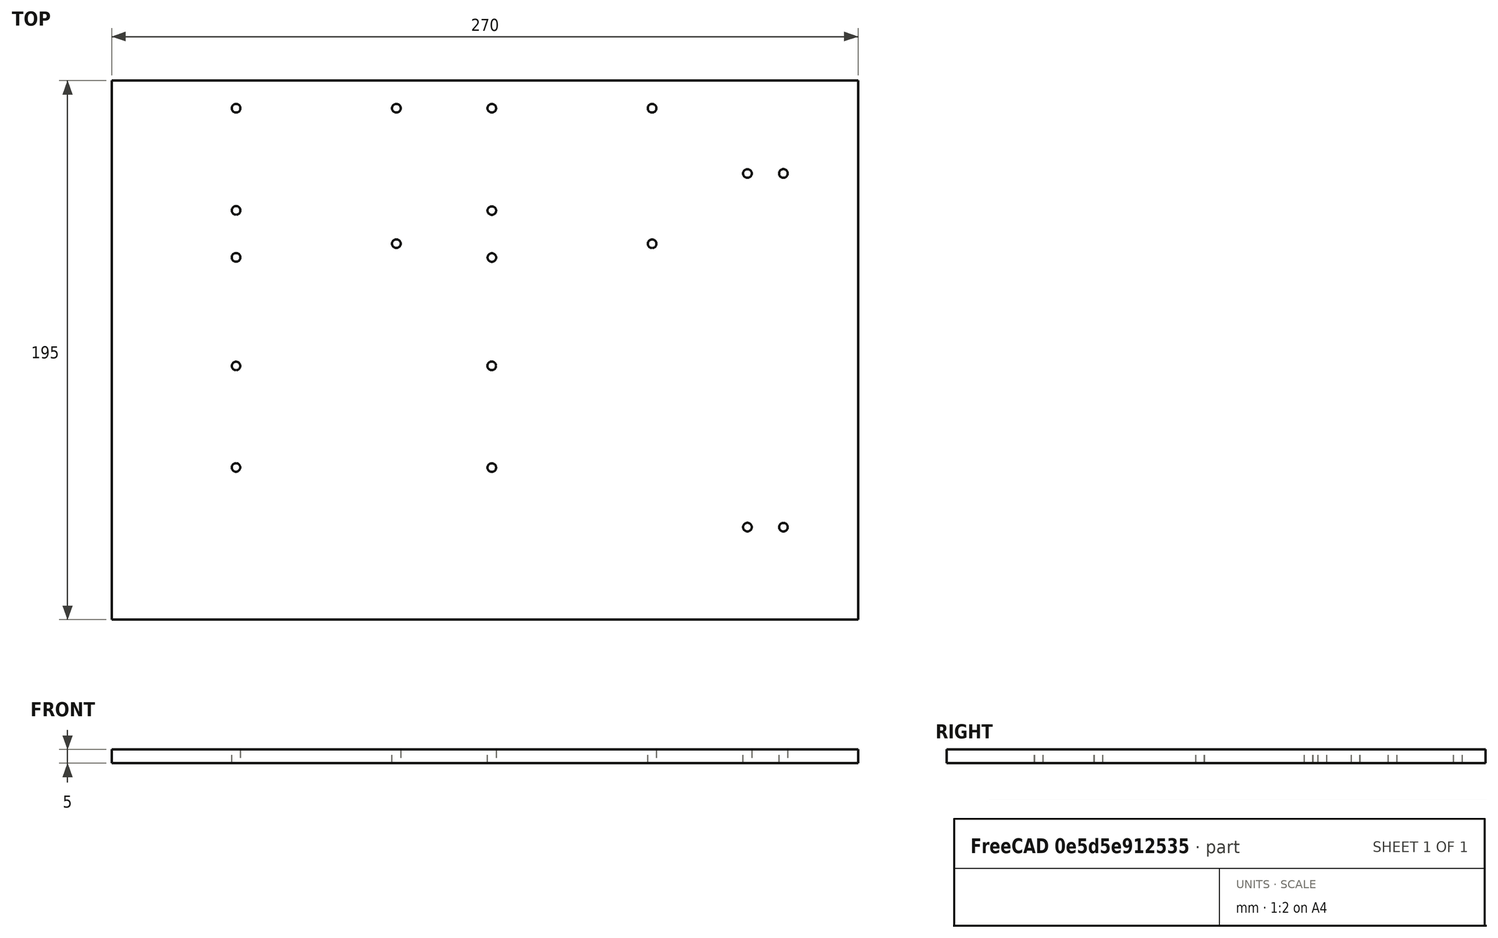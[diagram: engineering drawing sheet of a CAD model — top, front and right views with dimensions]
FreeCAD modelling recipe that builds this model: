
FCSTD DOCUMENT  (FreeCAD 0.16R6710 (Git))
Label: glassDesignQuarter
License: All rights reserved
LicenseURL: http://en.wikipedia.org/wiki/All_rights_reserved
objects: Drawing::FeatureViewPython×34, App::DocumentObjectGroup×5, Drawing::FeatureViewPart×2, Part::Box×1, Sketcher::SketchObject×1, PartDesign::Pocket×1, Drawing::FeaturePage×1
note: 4 computed .brp shape members not serialized (recipe doc carries the construction recipe); baked Part::Feature solids carry a one-line shape summary decoded from their .brp

FEATURE [Part::Box] Box002  label="1/4"
  Height = 5
  Length = 270
  Width = 195
FEATURE [Sketcher::SketchObject] Sketch032
  Placement = pos=(0,0,5) rot=(0,0,1;0rad)
  Support = -> Box002 [Face6]
  sketch-geometry (18):
    g0: Circle CenterX=45.0007 CenterY=185.02 CenterZ=0 NormalX=0 NormalY=0 NormalZ=1 Radius=1.5637
    g1: Circle CenterX=45.0164 CenterY=148.036 CenterZ=0 NormalX=0 NormalY=0 NormalZ=1 Radius=1.56346
    g2: Circle CenterX=44.9788 CenterY=131.047 CenterZ=0 NormalX=0 NormalY=0 NormalZ=1 Radius=1.57064
    g3: Circle CenterX=102.99 CenterY=185.022 CenterZ=0 NormalX=0 NormalY=0 NormalZ=1 Radius=1.5747
    g4: Circle CenterX=137.501 CenterY=185.021 CenterZ=0 NormalX=0 NormalY=0 NormalZ=1 Radius=1.55657
    g5: Circle CenterX=102.965 CenterY=136.023 CenterZ=0 NormalX=0 NormalY=0 NormalZ=1 Radius=1.56664
    g6: Circle CenterX=195.466 CenterY=185.025 CenterZ=0 NormalX=0 NormalY=0 NormalZ=1 Radius=1.56353
    g7: Circle CenterX=137.498 CenterY=147.976 CenterZ=0 NormalX=0 NormalY=0 NormalZ=1 Radius=1.55376
    g8: Circle CenterX=137.521 CenterY=130.994 CenterZ=0 NormalX=0 NormalY=0 NormalZ=1 Radius=1.55586
    g9: Circle CenterX=44.9819 CenterY=91.7501 CenterZ=0 NormalX=0 NormalY=0 NormalZ=1 Radius=1.53762
    g10: Circle CenterX=137.481 CenterY=91.7836 CenterZ=0 NormalX=0 NormalY=0 NormalZ=1 Radius=1.5579
    g11: Circle CenterX=44.9591 CenterY=55.0195 CenterZ=0 NormalX=0 NormalY=0 NormalZ=1 Radius=1.55028
    g12: Circle CenterX=137.5 CenterY=54.971 CenterZ=0 NormalX=0 NormalY=0 NormalZ=1 Radius=1.5621
    g13: Circle CenterX=195.5 CenterY=135.972 CenterZ=0 NormalX=0 NormalY=0 NormalZ=1 Radius=1.5583
    g14: Circle CenterX=229.972 CenterY=161.408 CenterZ=0 NormalX=0 NormalY=0 NormalZ=1 Radius=1.56999
    g15: Circle CenterX=242.978 CenterY=161.431 CenterZ=0 NormalX=0 NormalY=0 NormalZ=1 Radius=1.57387
    g16: Circle CenterX=229.973 CenterY=33.4261 CenterZ=0 NormalX=0 NormalY=0 NormalZ=1 Radius=1.57027
    g17: Circle CenterX=242.986 CenterY=33.4186 CenterZ=0 NormalX=0 NormalY=0 NormalZ=1 Radius=1.55472
FEATURE [PartDesign::Pocket] Pocket002
  Length = 5
  Sketch = -> Sketch032
  Type = 0
FEATURE [App::DocumentObjectGroup] Group  label="1/4U"
  Group = -> [Box002,Pocket002]
FEATURE [Drawing::FeatureViewPart] Ortho  label="Ortho_0_0"
  Direction = (0,0,1)
  HiddenWidth = 0.15
  LineWidth = 0.35
  Rotation = 0
  ShowHiddenLines = false
  ShowSmoothLines = false
  Source = -> Pocket002
  Tolerance = 0.05
  ViewResult = <g id="Ortho_0_0"\n   transform="rotate(0,120,297.67) translate(120,297.67) scale(1,1)"\n  >\n<g   stroke="rgb(0, 0, 0)"\n   stroke-width="0.35"\n   stroke-linecap="butt"\n   stroke-linejoin="miter"\n   fill="none"\n   transform="scale(1,-1)"\n  >\n<path id= "1" d=" M 0 0 L 0 195 " />\n<path id= "2" d=" M 0 0 L 270 0 " />\n<path id= "3" d=" M 0 195 L 270 195 " />\n<path id= "4" d=" M 270 0 L 270 195 " />\n<circle cx ="45.0164" cy ="148.036" r ="1.56346" /><circle cx ="44.9788" cy ="131.047" r ="1.57064" /><circle cx ="137.498" cy ="147.976" r ="1.55376" /><circle cx ="137.521" cy ="130.994" r ="1.55586" /><circle cx ="102.965" cy ="136.023" r ="1.56664" /><circle cx ="137.5" cy ="54.971" r ="1.5621" /><circle cx ="137.481" cy ="91.7836" r ="1.5579" /><circle cx ="44.9819" cy ="91.7501" r ="1.53762" /><circle cx ="44.9591" cy ="55.0195" r ="1.55028" /><circle cx ="229.973" cy ="33.4261" r ="1.57027" /><circle cx ="195.5" cy ="135.972" r ="1.5583" /><circle cx ="45.0007" cy ="185.02" r ="1.5637" /><circle cx ="137.501" cy ="185.021" r ="1.55657" /><circle cx ="102.99" cy ="185.022" r ="1.5747" /><circle cx ="229.972" cy ="161.408" r ="1.56999" /><circle cx ="195.466" cy ="185.025" r ="1.56353" /><circle cx ="242.986" cy ="33.4186" r ="1.55472" /><circle cx ="242.978" cy ="161.431" r ="1.57387" /></g>\n</g>
  Visible = true
  X = 120
  Y = 297.67
FEATURE [Drawing::FeatureViewPart] Ortho001  label="Ortho_0_-1"
  Direction = (0,-1,0)
  HiddenWidth = 0.15
  LineWidth = 0.35
  Rotation = 90
  ShowHiddenLines = false
  ShowSmoothLines = false
  Source = -> Pocket002
  Tolerance = 0.05
  ViewResult = <blob: 2655 chars omitted>
  Visible = true
  X = 120
  Y = 353.33
FEATURE [Drawing::FeatureViewPython] dim001  # drawing view (typed FeaturePython)
  Rotation = 0
  ViewResult = <g> \n  <line x1="120.000000" y1="102.670000" x2="120.000000" y2="94.000000" style="stroke:rgb(0,0,255);stroke-width:0.50" />\n<line x1="165.000700" y1="112.650000" x2="165.000700" y2="94.000000" style="stroke:rgb(0,0,255);stroke-width:0.50" />\n<line x1="120.000000" y1="95.000000" x2="165.000700" y2="95.000000" style="stroke:rgb(0,0,255);stroke-width:0.50" /> \n  <polygon points="165.000700,95.000000 162.000700,94.000000 161.000700,95.000000 162.000700,96.000000" style="fill:rgb(0,0,255);stroke:rgb(0,0,255);stroke-width:0" /><polygon points="120.000000,95.000000 123.000000,96.000000 124.000000,95.000000 123.000000,94.000000" style="fill:rgb(0,0,255);stroke:rgb(0,0,255);stroke-width:0" /> \n  <text x="135.000000" y="93.000000" font-family="inherit" font-size="6" fill="rgb(0,0,255)" text-anchor="inherit" transform="rotate(0.000000 135.000000,93.000000)" >45mm</text> </g>
  Visible = true
  X = 0
  Y = 0
  arrowL1 = 3
  arrowL2 = 1
  arrowW = 2
  arrow_scheme = 0
  autoPlaceOffset = 2
  autoPlaceText = false
  click1_x = 158
  click1_y = 95
  click2_x = 135
  click2_y = 93
  comma_decimal_place = false
  dimension_line_overshoot = 1
  gap_datum_points = 0
  halfDimension_linear = false
  lineColor = rgb(0,0,255)
  strokeWidth = 0.5
  textFormat_linear = 45mm
  textRenderer_color = rgb(0,0,255)
  textRenderer_family = inherit
  textRenderer_size = 6
  unit_custom_scale = 1
  unit_scheme = 0
FEATURE [Drawing::FeatureViewPython] dim002  # drawing view (typed FeaturePython)
  Rotation = 0
  ViewResult = <g> \n  <line x1="120.000000" y1="102.670000" x2="120.000000" y2="84.000000" style="stroke:rgb(0,0,255);stroke-width:0.50" />\n<line x1="222.990000" y1="112.648000" x2="222.990000" y2="84.000000" style="stroke:rgb(0,0,255);stroke-width:0.50" />\n<line x1="120.000000" y1="85.000000" x2="222.990000" y2="85.000000" style="stroke:rgb(0,0,255);stroke-width:0.50" /> \n  <polygon points="222.990000,85.000000 219.990000,84.000000 218.990000,85.000000 219.990000,86.000000" style="fill:rgb(0,0,255);stroke:rgb(0,0,255);stroke-width:0" /><polygon points="120.000000,85.000000 123.000000,86.000000 124.000000,85.000000 123.000000,84.000000" style="fill:rgb(0,0,255);stroke:rgb(0,0,255);stroke-width:0" /> \n  <text x="163.010000" y="83.000000" font-family="inherit" font-size="6" fill="rgb(0,0,255)" text-anchor="inherit" transform="rotate(0.000000 163.010000,83.000000)" >103mm</text> </g>
  Visible = true
  X = 0
  Y = 0
  arrowL1 = 3
  arrowL2 = 1
  arrowW = 2
  arrow_scheme = 0
  autoPlaceOffset = 2
  autoPlaceText = false
  click1_x = 212.354
  click1_y = 85
  click2_x = 163.01
  click2_y = 83
  comma_decimal_place = false
  dimension_line_overshoot = 1
  gap_datum_points = 0
  halfDimension_linear = false
  lineColor = rgb(0,0,255)
  strokeWidth = 0.5
  textFormat_linear = 103mm
  textRenderer_color = rgb(0,0,255)
  textRenderer_family = inherit
  textRenderer_size = 6
  unit_custom_scale = 1
  unit_scheme = 0
FEATURE [Drawing::FeatureViewPython] dim003  # drawing view (typed FeaturePython)
  Rotation = 0
  ViewResult = <g> \n  <line x1="120.000000" y1="102.670000" x2="120.000000" y2="74.000000" style="stroke:rgb(0,0,255);stroke-width:0.50" />\n<line x1="257.501000" y1="112.649000" x2="257.501000" y2="74.000000" style="stroke:rgb(0,0,255);stroke-width:0.50" />\n<line x1="120.000000" y1="75.000000" x2="257.501000" y2="75.000000" style="stroke:rgb(0,0,255);stroke-width:0.50" /> \n  <polygon points="257.501000,75.000000 254.501000,74.000000 253.501000,75.000000 254.501000,76.000000" style="fill:rgb(0,0,255);stroke:rgb(0,0,255);stroke-width:0" /><polygon points="120.000000,75.000000 123.000000,76.000000 124.000000,75.000000 123.000000,74.000000" style="fill:rgb(0,0,255);stroke:rgb(0,0,255);stroke-width:0" /> \n  <text x="174.190000" y="73.000000" font-family="inherit" font-size="6" fill="rgb(0,0,255)" text-anchor="inherit" transform="rotate(0.000000 174.190000,73.000000)" >137.5mm</text> </g>
  Visible = true
  X = 0
  Y = 0
  arrowL1 = 3
  arrowL2 = 1
  arrowW = 2
  arrow_scheme = 0
  autoPlaceOffset = 2
  autoPlaceText = false
  click1_x = 204.483
  click1_y = 75
  click2_x = 174.19
  click2_y = 73
  comma_decimal_place = false
  dimension_line_overshoot = 1
  gap_datum_points = 0
  halfDimension_linear = false
  lineColor = rgb(0,0,255)
  strokeWidth = 0.5
  textFormat_linear = 137.5mm
  textRenderer_color = rgb(0,0,255)
  textRenderer_family = inherit
  textRenderer_size = 6
  unit_custom_scale = 1
  unit_scheme = 0
FEATURE [Drawing::FeatureViewPython] dim004  # drawing view (typed FeaturePython)
  Rotation = 0
  ViewResult = <g> \n  <line x1="390.000000" y1="102.670000" x2="390.000000" y2="94.000000" style="stroke:rgb(0,0,255);stroke-width:0.50" />\n<line x1="362.978000" y1="136.239000" x2="362.978000" y2="94.000000" style="stroke:rgb(0,0,255);stroke-width:0.50" />\n<line x1="390.000000" y1="95.000000" x2="362.978000" y2="95.000000" style="stroke:rgb(0,0,255);stroke-width:0.50" /> \n  <polygon points="362.978000,95.000000 365.978000,96.000000 366.978000,95.000000 365.978000,94.000000" style="fill:rgb(0,0,255);stroke:rgb(0,0,255);stroke-width:0" /><polygon points="390.000000,95.000000 387.000000,94.000000 386.000000,95.000000 387.000000,96.000000" style="fill:rgb(0,0,255);stroke:rgb(0,0,255);stroke-width:0" /> \n  <text x="367.310000" y="93.000000" font-family="inherit" font-size="6" fill="rgb(0,0,255)" text-anchor="inherit" transform="rotate(0.000000 367.310000,93.000000)" >27mm</text> </g>
  Visible = true
  X = 0
  Y = 0
  arrowL1 = 3
  arrowL2 = 1
  arrowW = 2
  arrow_scheme = 0
  autoPlaceOffset = 2
  autoPlaceText = false
  click1_x = 366.142
  click1_y = 95
  click2_x = 367.31
  click2_y = 93
  comma_decimal_place = false
  dimension_line_overshoot = 1
  gap_datum_points = 0
  halfDimension_linear = false
  lineColor = rgb(0,0,255)
  strokeWidth = 0.5
  textFormat_linear = 27mm
  textRenderer_color = rgb(0,0,255)
  textRenderer_family = inherit
  textRenderer_size = 6
  unit_custom_scale = 1
  unit_scheme = 0
FEATURE [Drawing::FeatureViewPython] dim005  # drawing view (typed FeaturePython)
  Rotation = 0
  ViewResult = <g> \n  <line x1="349.972000" y1="136.262000" x2="349.972000" y2="84.000000" style="stroke:rgb(0,0,255);stroke-width:0.50" />\n<line x1="390.000000" y1="102.670000" x2="390.000000" y2="84.000000" style="stroke:rgb(0,0,255);stroke-width:0.50" />\n<line x1="349.972000" y1="85.000000" x2="390.000000" y2="85.000000" style="stroke:rgb(0,0,255);stroke-width:0.50" /> \n  <polygon points="390.000000,85.000000 387.000000,84.000000 386.000000,85.000000 387.000000,86.000000" style="fill:rgb(0,0,255);stroke:rgb(0,0,255);stroke-width:0" /><polygon points="349.972000,85.000000 352.972000,86.000000 353.972000,85.000000 352.972000,84.000000" style="fill:rgb(0,0,255);stroke:rgb(0,0,255);stroke-width:0" /> \n  <text x="360.130000" y="83.000000" font-family="inherit" font-size="6" fill="rgb(0,0,255)" text-anchor="inherit" transform="rotate(0.000000 360.130000,83.000000)" >40mm</text> </g>
  Visible = true
  X = 0
  Y = 0
  arrowL1 = 3
  arrowL2 = 1
  arrowW = 2
  arrow_scheme = 0
  autoPlaceOffset = 2
  autoPlaceText = false
  click1_x = 376.503
  click1_y = 85
  click2_x = 360.13
  click2_y = 83
  comma_decimal_place = false
  dimension_line_overshoot = 1
  gap_datum_points = 0
  halfDimension_linear = false
  lineColor = rgb(0,0,255)
  strokeWidth = 0.5
  textFormat_linear = 40mm
  textRenderer_color = rgb(0,0,255)
  textRenderer_family = inherit
  textRenderer_size = 6
  unit_custom_scale = 1
  unit_scheme = 0
FEATURE [Drawing::FeatureViewPython] dim006  # drawing view (typed FeaturePython)
  Rotation = 0
  ViewResult = <g> \n  <line x1="315.466000" y1="112.645000" x2="315.466000" y2="74.000000" style="stroke:rgb(0,0,255);stroke-width:0.50" />\n<line x1="390.000000" y1="102.670000" x2="390.000000" y2="74.000000" style="stroke:rgb(0,0,255);stroke-width:0.50" />\n<line x1="315.466000" y1="75.000000" x2="390.000000" y2="75.000000" style="stroke:rgb(0,0,255);stroke-width:0.50" /> \n  <polygon points="390.000000,75.000000 387.000000,74.000000 386.000000,75.000000 387.000000,76.000000" style="fill:rgb(0,0,255);stroke:rgb(0,0,255);stroke-width:0" /><polygon points="315.466000,75.000000 318.466000,76.000000 319.466000,75.000000 318.466000,74.000000" style="fill:rgb(0,0,255);stroke:rgb(0,0,255);stroke-width:0" /> \n  <text x="341.880000" y="73.000000" font-family="inherit" font-size="6" fill="rgb(0,0,255)" text-anchor="inherit" transform="rotate(0.000000 341.880000,73.000000)" >74.5mm</text> </g>
  Visible = true
  X = 0
  Y = 0
  arrowL1 = 3
  arrowL2 = 1
  arrowW = 2
  arrow_scheme = 0
  autoPlaceOffset = 2
  autoPlaceText = false
  click1_x = 387.475
  click1_y = 75
  click2_x = 341.88
  click2_y = 73
  comma_decimal_place = false
  dimension_line_overshoot = 1
  gap_datum_points = 0
  halfDimension_linear = false
  lineColor = rgb(0,0,255)
  strokeWidth = 0.5
  textFormat_linear = 74.5mm
  textRenderer_color = rgb(0,0,255)
  textRenderer_family = inherit
  textRenderer_size = 6
  unit_custom_scale = 1
  unit_scheme = 0
FEATURE [App::DocumentObjectGroup] Group001  label="TopDim"
  Group = -> [dim001,dim002,dim003,dim004,dim005,dim006]
FEATURE [Drawing::FeatureViewPython] dim007  # drawing view (typed FeaturePython)
  Rotation = 0
  ViewResult = <g> \n  <line x1="120.000000" y1="102.670000" x2="114.000000" y2="102.670000" style="stroke:rgb(0,0,255);stroke-width:0.50" />\n<line x1="165.000700" y1="112.650000" x2="114.000000" y2="112.650000" style="stroke:rgb(0,0,255);stroke-width:0.50" />\n<line x1="115.000000" y1="102.670000" x2="115.000000" y2="112.650000" style="stroke:rgb(0,0,255);stroke-width:0.50" /> \n  <polygon points="115.000000,112.650000 114.000000,115.650000 115.000000,116.650000 116.000000,115.650000" style="fill:rgb(0,0,255);stroke:rgb(0,0,255);stroke-width:0" /><polygon points="115.000000,102.670000 116.000000,99.670000 115.000000,98.670000 114.000000,99.670000" style="fill:rgb(0,0,255);stroke:rgb(0,0,255);stroke-width:0" /> \n  <text x="113.000000" y="121.500000" font-family="inherit" font-size="6" fill="rgb(0,0,255)" text-anchor="inherit" transform="rotate(-90.000000 113.000000,121.500000)" >10mm</text> </g>
  Visible = true
  X = 0
  Y = 0
  arrowL1 = 3
  arrowL2 = 1
  arrowW = 2
  arrow_scheme = 0
  autoPlaceOffset = 2
  autoPlaceText = false
  click1_x = 115
  click1_y = 110
  click2_x = 113
  click2_y = 121.5
  comma_decimal_place = false
  dimension_line_overshoot = 1
  gap_datum_points = 0
  halfDimension_linear = false
  lineColor = rgb(0,0,255)
  strokeWidth = 0.5
  textFormat_linear = 10mm
  textRenderer_color = rgb(0,0,255)
  textRenderer_family = inherit
  textRenderer_size = 6
  unit_custom_scale = 1
  unit_scheme = 0
FEATURE [Drawing::FeatureViewPython] dim008  # drawing view (typed FeaturePython)
  Rotation = 0
  ViewResult = <g> \n  <line x1="120.000000" y1="102.670000" x2="104.000000" y2="102.670000" style="stroke:rgb(0,0,255);stroke-width:0.50" />\n<line x1="165.016400" y1="149.634000" x2="104.000000" y2="149.634000" style="stroke:rgb(0,0,255);stroke-width:0.50" />\n<line x1="105.000000" y1="102.670000" x2="105.000000" y2="149.634000" style="stroke:rgb(0,0,255);stroke-width:0.50" /> \n  <polygon points="105.000000,149.634000 106.000000,146.634000 105.000000,145.634000 104.000000,146.634000" style="fill:rgb(0,0,255);stroke:rgb(0,0,255);stroke-width:0" /><polygon points="105.000000,102.670000 104.000000,105.670000 105.000000,106.670000 106.000000,105.670000" style="fill:rgb(0,0,255);stroke:rgb(0,0,255);stroke-width:0" /> \n  <text x="103.000000" y="132.385854" font-family="inherit" font-size="6" fill="rgb(0,0,255)" text-anchor="inherit" transform="rotate(-90.000000 103.000000,132.385854)" >47mm</text> </g>
  Visible = true
  X = 0
  Y = 0
  arrowL1 = 3
  arrowL2 = 1
  arrowW = 2
  arrow_scheme = 0
  autoPlaceOffset = 2
  autoPlaceText = false
  click1_x = 105
  click1_y = 141.897
  click2_x = 103
  click2_y = 132.386
  comma_decimal_place = false
  dimension_line_overshoot = 1
  gap_datum_points = 0
  halfDimension_linear = false
  lineColor = rgb(0,0,255)
  strokeWidth = 0.5
  textFormat_linear = 47mm
  textRenderer_color = rgb(0,0,255)
  textRenderer_family = inherit
  textRenderer_size = 6
  unit_custom_scale = 1
  unit_scheme = 0
FEATURE [Drawing::FeatureViewPython] dim010  # drawing view (typed FeaturePython)
  Rotation = 0
  ViewResult = <g> \n  <line x1="120.000000" y1="297.670000" x2="114.000000" y2="297.670000" style="stroke:rgb(0,0,255);stroke-width:0.50" />\n<line x1="164.959100" y1="242.650500" x2="114.000000" y2="242.650500" style="stroke:rgb(0,0,255);stroke-width:0.50" />\n<line x1="115.000000" y1="297.670000" x2="115.000000" y2="242.650500" style="stroke:rgb(0,0,255);stroke-width:0.50" /> \n  <polygon points="115.000000,242.650500 114.000000,245.650500 115.000000,246.650500 116.000000,245.650500" style="fill:rgb(0,0,255);stroke:rgb(0,0,255);stroke-width:0" /><polygon points="115.000000,297.670000 116.000000,294.670000 115.000000,293.670000 114.000000,294.670000" style="fill:rgb(0,0,255);stroke:rgb(0,0,255);stroke-width:0" /> \n  <text x="113.000000" y="279.890000" font-family="inherit" font-size="6" fill="rgb(0,0,255)" text-anchor="inherit" transform="rotate(-90.000000 113.000000,279.890000)" >55mm</text> </g>
  Visible = true
  X = 0
  Y = 0
  arrowL1 = 3
  arrowL2 = 1
  arrowW = 2
  arrow_scheme = 0
  autoPlaceOffset = 2
  autoPlaceText = false
  click1_x = 115
  click1_y = 268.54
  click2_x = 113
  click2_y = 279.89
  comma_decimal_place = false
  dimension_line_overshoot = 1
  gap_datum_points = 0
  halfDimension_linear = false
  lineColor = rgb(0,0,255)
  strokeWidth = 0.5
  textFormat_linear = 55mm
  textRenderer_color = rgb(0,0,255)
  textRenderer_family = inherit
  textRenderer_size = 6
  unit_custom_scale = 1
  unit_scheme = 0
FEATURE [Drawing::FeatureViewPython] dim011  # drawing view (typed FeaturePython)
  Rotation = 0
  ViewResult = <g> \n  <line x1="164.981900" y1="205.919900" x2="104.000000" y2="205.919900" style="stroke:rgb(0,0,255);stroke-width:0.50" />\n<line x1="120.000000" y1="297.670000" x2="104.000000" y2="297.670000" style="stroke:rgb(0,0,255);stroke-width:0.50" />\n<line x1="105.000000" y1="205.919900" x2="105.000000" y2="297.670000" style="stroke:rgb(0,0,255);stroke-width:0.50" /> \n  <polygon points="105.000000,297.670000 106.000000,294.670000 105.000000,293.670000 104.000000,294.670000" style="fill:rgb(0,0,255);stroke:rgb(0,0,255);stroke-width:0" /><polygon points="105.000000,205.919900 104.000000,208.919900 105.000000,209.919900 106.000000,208.919900" style="fill:rgb(0,0,255);stroke:rgb(0,0,255);stroke-width:0" /> \n  <text x="103.000000" y="260.591529" font-family="inherit" font-size="6" fill="rgb(0,0,255)" text-anchor="inherit" transform="rotate(-90.000000 103.000000,260.591529)" >91.75mm</text> </g>
  Visible = true
  X = 0
  Y = 0
  arrowL1 = 3
  arrowL2 = 1
  arrowW = 2
  arrow_scheme = 0
  autoPlaceOffset = 2
  autoPlaceText = false
  click1_x = 105
  click1_y = 294.543
  click2_x = 103
  click2_y = 260.592
  comma_decimal_place = false
  dimension_line_overshoot = 1
  gap_datum_points = 0
  halfDimension_linear = false
  lineColor = rgb(0,0,255)
  strokeWidth = 0.5
  textFormat_linear = 91.75mm
  textRenderer_color = rgb(0,0,255)
  textRenderer_family = inherit
  textRenderer_size = 6
  unit_custom_scale = 1
  unit_scheme = 0
FEATURE [Drawing::FeatureViewPython] dim012  # drawing view (typed FeaturePython)
  Rotation = 0
  ViewResult = <g> \n  <line x1="164.978800" y1="166.623000" x2="94.000000" y2="166.623000" style="stroke:rgb(0,0,255);stroke-width:0.50" />\n<line x1="120.000000" y1="297.670000" x2="94.000000" y2="297.670000" style="stroke:rgb(0,0,255);stroke-width:0.50" />\n<line x1="95.000000" y1="166.623000" x2="95.000000" y2="297.670000" style="stroke:rgb(0,0,255);stroke-width:0.50" /> \n  <polygon points="95.000000,297.670000 96.000000,294.670000 95.000000,293.670000 94.000000,294.670000" style="fill:rgb(0,0,255);stroke:rgb(0,0,255);stroke-width:0" /><polygon points="95.000000,166.623000 94.000000,169.623000 95.000000,170.623000 96.000000,169.623000" style="fill:rgb(0,0,255);stroke:rgb(0,0,255);stroke-width:0" /> \n  <text x="93.000000" y="242.884703" font-family="inherit" font-size="6" fill="rgb(0,0,255)" text-anchor="inherit" transform="rotate(-90.000000 93.000000,242.884703)" >131mm</text> </g>
  Visible = true
  X = 0
  Y = 0
  arrowL1 = 3
  arrowL2 = 1
  arrowW = 2
  arrow_scheme = 0
  autoPlaceOffset = 2
  autoPlaceText = false
  click1_x = 95
  click1_y = 294.216
  click2_x = 93
  click2_y = 242.885
  comma_decimal_place = false
  dimension_line_overshoot = 1
  gap_datum_points = 0
  halfDimension_linear = false
  lineColor = rgb(0,0,255)
  strokeWidth = 0.5
  textFormat_linear = 131mm
  textRenderer_color = rgb(0,0,255)
  textRenderer_family = inherit
  textRenderer_size = 6
  unit_custom_scale = 1
  unit_scheme = 0
FEATURE [Drawing::FeatureViewPython] dim013  # drawing view (typed FeaturePython)
  Rotation = 0
  ViewResult = <g> \n  <line x1="390.000000" y1="102.670000" x2="411.000000" y2="102.670000" style="stroke:rgb(0,0,255);stroke-width:0.50" />\n<line x1="362.978000" y1="136.239000" x2="411.000000" y2="136.239000" style="stroke:rgb(0,0,255);stroke-width:0.50" />\n<line x1="410.000000" y1="102.670000" x2="410.000000" y2="136.239000" style="stroke:rgb(0,0,255);stroke-width:0.50" /> \n  <polygon points="410.000000,136.239000 411.000000,133.239000 410.000000,132.239000 409.000000,133.239000" style="fill:rgb(0,0,255);stroke:rgb(0,0,255);stroke-width:0" /><polygon points="410.000000,102.670000 409.000000,105.670000 410.000000,106.670000 411.000000,105.670000" style="fill:rgb(0,0,255);stroke:rgb(0,0,255);stroke-width:0" /> \n  <text x="408.000000" y="129.280000" font-family="inherit" font-size="6" fill="rgb(0,0,255)" text-anchor="inherit" transform="rotate(-90.000000 408.000000,129.280000)" >33.5mm</text> </g>
  Visible = true
  X = 0
  Y = 0
  arrowL1 = 3
  arrowL2 = 1
  arrowW = 2
  arrow_scheme = 0
  autoPlaceOffset = 2
  autoPlaceText = false
  click1_x = 410
  click1_y = 129.534
  click2_x = 408
  click2_y = 129.28
  comma_decimal_place = false
  dimension_line_overshoot = 1
  gap_datum_points = 0
  halfDimension_linear = false
  lineColor = rgb(0,0,255)
  strokeWidth = 0.5
  textFormat_linear = 33.5mm
  textRenderer_color = rgb(0,0,255)
  textRenderer_family = inherit
  textRenderer_size = 6
  unit_custom_scale = 1
  unit_scheme = 0
FEATURE [Drawing::FeatureViewPython] dim014  # drawing view (typed FeaturePython)
  Rotation = 0
  ViewResult = <g> \n  <line x1="390.000000" y1="297.670000" x2="411.000000" y2="297.670000" style="stroke:rgb(0,0,255);stroke-width:0.50" />\n<line x1="362.986000" y1="264.251400" x2="411.000000" y2="264.251400" style="stroke:rgb(0,0,255);stroke-width:0.50" />\n<line x1="410.000000" y1="297.670000" x2="410.000000" y2="264.251400" style="stroke:rgb(0,0,255);stroke-width:0.50" /> \n  <polygon points="410.000000,264.251400 409.000000,267.251400 410.000000,268.251400 411.000000,267.251400" style="fill:rgb(0,0,255);stroke:rgb(0,0,255);stroke-width:0" /><polygon points="410.000000,297.670000 411.000000,294.670000 410.000000,293.670000 409.000000,294.670000" style="fill:rgb(0,0,255);stroke:rgb(0,0,255);stroke-width:0" /> \n  <text x="408.000000" y="292.690000" font-family="inherit" font-size="6" fill="rgb(0,0,255)" text-anchor="inherit" transform="rotate(-90.000000 408.000000,292.690000)" >33.5mm</text> </g>
  Visible = true
  X = 0
  Y = 0
  arrowL1 = 3
  arrowL2 = 1
  arrowW = 2
  arrow_scheme = 0
  autoPlaceOffset = 2
  autoPlaceText = false
  click1_x = 410
  click1_y = 274.672
  click2_x = 408
  click2_y = 292.69
  comma_decimal_place = false
  dimension_line_overshoot = 1
  gap_datum_points = 0
  halfDimension_linear = false
  lineColor = rgb(0,0,255)
  strokeWidth = 0.5
  textFormat_linear = 33.5mm
  textRenderer_color = rgb(0,0,255)
  textRenderer_family = inherit
  textRenderer_size = 6
  unit_custom_scale = 1
  unit_scheme = 0
FEATURE [Drawing::FeatureViewPython] dim015  # drawing view (typed FeaturePython)
  Rotation = 0
  ViewResult = <g> \n  <line x1="390.000000" y1="297.670000" x2="441.000000" y2="297.670000" style="stroke:rgb(0,0,255);stroke-width:0.50" />\n<line x1="390.000000" y1="102.670000" x2="441.000000" y2="102.670000" style="stroke:rgb(0,0,255);stroke-width:0.50" />\n<line x1="440.000000" y1="297.670000" x2="440.000000" y2="102.670000" style="stroke:rgb(0,0,255);stroke-width:0.50" /> \n  <polygon points="440.000000,102.670000 439.000000,105.670000 440.000000,106.670000 441.000000,105.670000" style="fill:rgb(0,0,255);stroke:rgb(0,0,255);stroke-width:0" /><polygon points="440.000000,297.670000 441.000000,294.670000 440.000000,293.670000 439.000000,294.670000" style="fill:rgb(0,0,255);stroke:rgb(0,0,255);stroke-width:0" /> \n  <text x="438.000000" y="208.320000" font-family="inherit" font-size="6" fill="rgb(0,0,255)" text-anchor="inherit" transform="rotate(-90.000000 438.000000,208.320000)" >195mm</text> </g>
  Visible = true
  X = 0
  Y = 0
  arrowL1 = 3
  arrowL2 = 1
  arrowW = 2
  arrow_scheme = 0
  autoPlaceOffset = 2
  autoPlaceText = false
  click1_x = 440
  click1_y = 208.26
  click2_x = 438
  click2_y = 208.32
  comma_decimal_place = false
  dimension_line_overshoot = 1
  gap_datum_points = 0
  halfDimension_linear = false
  lineColor = rgb(0,0,255)
  strokeWidth = 0.5
  textFormat_linear = %(value)3.0fmm
  textRenderer_color = rgb(0,0,255)
  textRenderer_family = inherit
  textRenderer_size = 6
  unit_custom_scale = 1
  unit_scheme = 0
FEATURE [App::DocumentObjectGroup] Group003  label="RightDim"
  Group = -> [dim013,dim014,dim015]
FEATURE [Drawing::FeatureViewPython] centerLines001  # drawing view (typed FeaturePython)
  Rotation = 0
  ViewResult = <g transform="scale(1.000000,1.000000)" stroke="rgb(0,0,255)"  stroke-width="0.320000" > <path d="M 165.000700,112.650000 L 165.000700,115.650000 M 165.000700,117.650000 L 165.000700,123.650000 M 165.000700,125.650000 L 165.000700,128.650000 M 165.000700,130.650000 L 165.000700,136.650000 M 165.000700,138.650000 L 165.000700,141.650000 M 165.000700,143.650000 L 165.000700,149.650000 M 165.000700,151.650000 L 165.000700,154.650000 M 165.000700,156.650000 L 165.000700,162.650000 M 165.000700,164.650000 L 165.000700,167.650000 M 165.000700,169.650000 L 165.000700,175.650000 M 165.000700,177.650000 L 165.000700,180.650000 M 165.000700,182.650000 L 165.000700,188.650000 M 165.000700,190.650000 L 165.000700,193.650000 M 165.000700,195.650000 L 165.000700,201.650000 M 165.000700,203.650000 L 165.000700,206.650000 M 165.000700,208.650000 L 165.000700,214.650000 M 165.000700,216.650000 L 165.000700,219.650000 M 165.000700,221.650000 L 165.000700,227.650000 M 165.000700,229.650000 L 165.000700,232.650000 M 165.000700,234.650000 L 165.000700,240.650000 "/>\n<path d="M 165.000700,112.650000 L 165.000700,115.650000 M 165.000700,117.650000 L 165.000700,123.650000 M 165.000700,125.650000 L 165.000700,128.650000 M 165.000700,130.650000 L 165.000700,136.650000 M 165.000700,138.650000 L 165.000700,141.650000 M 165.000700,143.650000 L 165.000700,149.650000 M 165.000700,151.650000 L 165.000700,154.650000 M 165.000700,156.650000 L 165.000700,162.650000 M 165.000700,164.650000 L 165.000700,167.650000 M 165.000700,169.650000 L 165.000700,175.650000 M 165.000700,177.650000 L 165.000700,180.650000 M 165.000700,182.650000 L 165.000700,188.650000 M 165.000700,190.650000 L 165.000700,193.650000 M 165.000700,195.650000 L 165.000700,201.650000 M 165.000700,203.650000 L 165.000700,206.650000 M 165.000700,208.650000 L 165.000700,214.650000 M 165.000700,216.650000 L 165.000700,219.650000 M 165.000700,221.650000 L 165.000700,227.650000 "/> </g> 
  Visible = true
  X = 0
  Y = 0
  centerLine_color = rgb(0,0,255)
  centerLine_len_dash = 6
  centerLine_len_dot = 3
  centerLine_len_gap = 2
  centerLine_width = 0.32
  click1_x = 166.298
  click1_y = 242.486
  click2_x = 169.445
  click2_y = 227.897
FEATURE [Drawing::FeatureViewPython] centerLines002  # drawing view (typed FeaturePython)
  Rotation = 0
  ViewResult = <g transform="scale(1.000000,1.000000)" stroke="rgb(0,0,255)"  stroke-width="0.320000" > <path d="M 222.990000,112.648000 L 222.990000,115.648000 M 222.990000,117.648000 L 222.990000,123.648000 M 222.990000,125.648000 L 222.990000,128.648000 M 222.990000,130.648000 L 222.990000,136.648000 M 222.990000,138.648000 L 222.990000,141.648000 M 222.990000,143.648000 L 222.990000,149.648000 M 222.990000,151.648000 L 222.990000,154.648000 M 222.990000,156.648000 L 222.990000,162.648000 "/>\n<path d="M 222.990000,112.648000 L 222.990000,115.648000 M 222.990000,117.648000 L 222.990000,123.648000 M 222.990000,125.648000 L 222.990000,128.648000 M 222.990000,130.648000 L 222.990000,136.648000 M 222.990000,138.648000 L 222.990000,141.648000 M 222.990000,143.648000 L 222.990000,149.648000 "/> </g> 
  Visible = true
  X = 0
  Y = 0
  centerLine_color = rgb(0,0,255)
  centerLine_len_dash = 6
  centerLine_len_dot = 3
  centerLine_len_gap = 2
  centerLine_width = 0.32
  click1_x = 224.877
  click1_y = 162.738
  click2_x = 227.341
  click2_y = 150.66
FEATURE [Drawing::FeatureViewPython] centerLines003  # drawing view (typed FeaturePython)
  Rotation = 0
  ViewResult = <g transform="scale(1.000000,1.000000)" stroke="rgb(0,0,255)"  stroke-width="0.320000" > <path d="M 257.501000,112.649000 L 257.501000,115.649000 M 257.501000,117.649000 L 257.501000,123.649000 M 257.501000,125.649000 L 257.501000,128.649000 M 257.501000,130.649000 L 257.501000,136.649000 M 257.501000,138.649000 L 257.501000,141.649000 M 257.501000,143.649000 L 257.501000,149.649000 M 257.501000,151.649000 L 257.501000,154.649000 M 257.501000,156.649000 L 257.501000,162.649000 M 257.501000,164.649000 L 257.501000,167.649000 M 257.501000,169.649000 L 257.501000,175.649000 M 257.501000,177.649000 L 257.501000,180.649000 M 257.501000,182.649000 L 257.501000,188.649000 M 257.501000,190.649000 L 257.501000,193.649000 M 257.501000,195.649000 L 257.501000,201.649000 M 257.501000,203.649000 L 257.501000,206.649000 M 257.501000,208.649000 L 257.501000,214.649000 M 257.501000,216.649000 L 257.501000,219.649000 M 257.501000,221.649000 L 257.501000,227.649000 M 257.501000,229.649000 L 257.501000,232.649000 M 257.501000,234.649000 L 257.501000,240.649000 M 257.501000,242.649000 L 257.501000,242.764475 "/>\n<path d="M 257.501000,112.649000 L 257.501000,115.649000 M 257.501000,117.649000 L 257.501000,123.649000 M 257.501000,125.649000 L 257.501000,128.649000 M 257.501000,130.649000 L 257.501000,136.649000 M 257.501000,138.649000 L 257.501000,141.649000 M 257.501000,143.649000 L 257.501000,149.649000 M 257.501000,151.649000 L 257.501000,154.649000 M 257.501000,156.649000 L 257.501000,162.649000 M 257.501000,164.649000 L 257.501000,167.649000 M 257.501000,169.649000 L 257.501000,175.649000 M 257.501000,177.649000 L 257.501000,180.649000 M 257.501000,182.649000 L 257.501000,188.649000 M 257.501000,190.649000 L 257.501000,193.649000 M 257.501000,195.649000 L 257.501000,201.649000 M 257.501000,203.649000 L 257.501000,206.649000 M 257.501000,208.649000 L 257.501000,214.649000 M 257.501000,216.649000 L 257.501000,219.649000 "/> </g> 
  Visible = true
  X = 0
  Y = 0
  centerLine_color = rgb(0,0,255)
  centerLine_len_dash = 6
  centerLine_len_dot = 3
  centerLine_len_gap = 2
  centerLine_width = 0.32
  click1_x = 258.692
  click1_y = 242.764
  click2_x = 264.185
  click2_y = 221.481
FEATURE [Drawing::FeatureViewPython] centerLines004  # drawing view (typed FeaturePython)
  Rotation = 0
  ViewResult = <g transform="scale(1.000000,1.000000)" stroke="rgb(0,0,255)"  stroke-width="0.320000" > <path d="M 315.466000,112.645000 L 315.466000,115.645000 M 315.466000,117.645000 L 315.466000,123.645000 M 315.466000,125.645000 L 315.466000,128.645000 M 315.466000,130.645000 L 315.466000,136.645000 M 315.466000,138.645000 L 315.466000,141.645000 M 315.466000,143.645000 L 315.466000,149.645000 M 315.466000,151.645000 L 315.466000,154.645000 M 315.466000,156.645000 L 315.466000,162.579119 "/>\n<path d="M 315.466000,112.645000 L 315.466000,115.645000 M 315.466000,117.645000 L 315.466000,123.645000 M 315.466000,125.645000 L 315.466000,128.645000 M 315.466000,130.645000 L 315.466000,136.645000 M 315.466000,138.645000 L 315.466000,141.645000 M 315.466000,143.645000 L 315.466000,144.461798 "/> </g> 
  Visible = true
  X = 0
  Y = 0
  centerLine_color = rgb(0,0,255)
  centerLine_len_dash = 6
  centerLine_len_dot = 3
  centerLine_len_gap = 2
  centerLine_width = 0.32
  click1_x = 319.628
  click1_y = 162.579
  click2_x = 322.012
  click2_y = 144.462
FEATURE [Drawing::FeatureViewPython] centerLines005  # drawing view (typed FeaturePython)
  Rotation = 0
  ViewResult = <g transform="scale(1.000000,1.000000)" stroke="rgb(0,0,255)"  stroke-width="0.320000" > <path d="M 349.972000,136.262000 L 349.972000,139.262000 M 349.972000,141.262000 L 349.972000,147.262000 M 349.972000,149.262000 L 349.972000,152.262000 M 349.972000,154.262000 L 349.972000,160.262000 M 349.972000,162.262000 L 349.972000,165.262000 M 349.972000,167.262000 L 349.972000,173.262000 M 349.972000,175.262000 L 349.972000,178.262000 M 349.972000,180.262000 L 349.972000,186.262000 M 349.972000,188.262000 L 349.972000,191.262000 M 349.972000,193.262000 L 349.972000,199.262000 M 349.972000,201.262000 L 349.972000,204.262000 M 349.972000,206.262000 L 349.972000,212.262000 M 349.972000,214.262000 L 349.972000,217.262000 M 349.972000,219.262000 L 349.972000,225.262000 M 349.972000,227.262000 L 349.972000,230.262000 M 349.972000,232.262000 L 349.972000,238.262000 M 349.972000,240.262000 L 349.972000,243.262000 M 349.972000,245.262000 L 349.972000,251.262000 M 349.972000,253.262000 L 349.972000,256.262000 M 349.972000,258.262000 L 349.972000,264.262000 "/>\n<path d="M 349.972000,136.262000 L 349.972000,139.262000 M 349.972000,141.262000 L 349.972000,147.262000 M 349.972000,149.262000 L 349.972000,152.262000 M 349.972000,154.262000 L 349.972000,160.262000 M 349.972000,162.262000 L 349.972000,165.262000 M 349.972000,167.262000 L 349.972000,173.262000 M 349.972000,175.262000 L 349.972000,178.262000 M 349.972000,180.262000 L 349.972000,186.262000 M 349.972000,188.262000 L 349.972000,191.262000 M 349.972000,193.262000 L 349.972000,199.262000 M 349.972000,201.262000 L 349.972000,204.262000 M 349.972000,206.262000 L 349.972000,212.262000 M 349.972000,214.262000 L 349.972000,217.262000 M 349.972000,219.262000 L 349.972000,225.262000 M 349.972000,227.262000 L 349.972000,230.262000 M 349.972000,232.262000 L 349.972000,238.262000 M 349.972000,240.262000 L 349.972000,243.262000 "/> </g> 
  Visible = true
  X = 0
  Y = 0
  centerLine_color = rgb(0,0,255)
  centerLine_len_dash = 6
  centerLine_len_dot = 3
  centerLine_len_gap = 2
  centerLine_width = 0.32
  click1_x = 352.746
  click1_y = 264.272
  click2_x = 354.417
  click2_y = 244.739
FEATURE [Drawing::FeatureViewPython] centerLines006  # drawing view (typed FeaturePython)
  Rotation = 0
  ViewResult = <g transform="scale(1.000000,1.000000)" stroke="rgb(0,0,255)"  stroke-width="0.320000" > <path d="M 362.978000,136.239000 L 362.978000,139.239000 M 362.978000,141.239000 L 362.978000,147.239000 M 362.978000,149.239000 L 362.978000,152.239000 M 362.978000,154.239000 L 362.978000,160.239000 M 362.978000,162.239000 L 362.978000,165.239000 M 362.978000,167.239000 L 362.978000,173.239000 M 362.978000,175.239000 L 362.978000,178.239000 M 362.978000,180.239000 L 362.978000,186.239000 M 362.978000,188.239000 L 362.978000,191.239000 M 362.978000,193.239000 L 362.978000,199.239000 M 362.978000,201.239000 L 362.978000,204.239000 M 362.978000,206.239000 L 362.978000,212.239000 M 362.978000,214.239000 L 362.978000,217.239000 M 362.978000,219.239000 L 362.978000,225.239000 M 362.978000,227.239000 L 362.978000,230.239000 M 362.978000,232.239000 L 362.978000,238.239000 M 362.978000,240.239000 L 362.978000,243.239000 M 362.978000,245.239000 L 362.978000,251.239000 M 362.978000,253.239000 L 362.978000,256.239000 M 362.978000,258.239000 L 362.978000,264.239000 "/>\n<path d="M 362.978000,136.239000 L 362.978000,139.239000 M 362.978000,141.239000 L 362.978000,147.239000 M 362.978000,149.239000 L 362.978000,152.239000 M 362.978000,154.239000 L 362.978000,160.239000 M 362.978000,162.239000 L 362.978000,165.239000 M 362.978000,167.239000 L 362.978000,173.239000 M 362.978000,175.239000 L 362.978000,178.239000 M 362.978000,180.239000 L 362.978000,186.239000 M 362.978000,188.239000 L 362.978000,191.239000 M 362.978000,193.239000 L 362.978000,199.239000 M 362.978000,201.239000 L 362.978000,204.239000 M 362.978000,206.239000 L 362.978000,212.239000 M 362.978000,214.239000 L 362.978000,217.239000 M 362.978000,219.239000 L 362.978000,225.239000 M 362.978000,227.239000 L 362.978000,230.239000 M 362.978000,232.239000 L 362.978000,238.239000 M 362.978000,240.239000 L 362.978000,243.239000 "/> </g> 
  Visible = true
  X = 0
  Y = 0
  centerLine_color = rgb(0,0,255)
  centerLine_len_dash = 6
  centerLine_len_dot = 3
  centerLine_len_gap = 2
  centerLine_width = 0.32
  click1_x = 367.991
  click1_y = 264.551
  click2_x = 370.051
  click2_y = 244.527
FEATURE [Drawing::FeatureViewPython] centerLines007  # drawing view (typed FeaturePython)
  Rotation = 0
  ViewResult = <blob: 2328 chars omitted>
  Visible = true
  X = 0
  Y = 0
  centerLine_color = rgb(0,0,255)
  centerLine_len_dash = 6
  centerLine_len_dot = 3
  centerLine_len_gap = 2
  centerLine_width = 0.32
  click1_x = 315.151
  click1_y = 114.075
  click2_x = 302.516
  click2_y = 112.27
FEATURE [Drawing::FeatureViewPython] centerLines008  # drawing view (typed FeaturePython)
  Rotation = 0
  ViewResult = <g transform="scale(1.000000,1.000000)" stroke="rgb(0,0,255)"  stroke-width="0.320000" > <path d="M 165.016400,149.634000 L 168.016400,149.634000 M 170.016400,149.634000 L 176.016400,149.634000 M 178.016400,149.634000 L 181.016400,149.634000 M 183.016400,149.634000 L 189.016400,149.634000 M 191.016400,149.634000 L 194.016400,149.634000 M 196.016400,149.634000 L 202.016400,149.634000 M 204.016400,149.634000 L 207.016400,149.634000 M 209.016400,149.634000 L 215.016400,149.634000 M 217.016400,149.634000 L 220.016400,149.634000 M 222.016400,149.634000 L 228.016400,149.634000 M 230.016400,149.634000 L 233.016400,149.634000 M 235.016400,149.634000 L 241.016400,149.634000 M 243.016400,149.634000 L 246.016400,149.634000 M 248.016400,149.634000 L 254.016400,149.634000 M 256.016400,149.634000 L 257.656718,149.634000 "/>\n<path d="M 165.016400,149.634000 L 168.016400,149.634000 M 170.016400,149.634000 L 176.016400,149.634000 M 178.016400,149.634000 L 181.016400,149.634000 M 183.016400,149.634000 L 189.016400,149.634000 M 191.016400,149.634000 L 194.016400,149.634000 M 196.016400,149.634000 L 202.016400,149.634000 M 204.016400,149.634000 L 207.016400,149.634000 M 209.016400,149.634000 L 215.016400,149.634000 M 217.016400,149.634000 L 220.016400,149.634000 M 222.016400,149.634000 L 228.016400,149.634000 M 230.016400,149.634000 L 233.016400,149.634000 M 235.016400,149.634000 L 241.016400,149.634000 "/> </g> 
  Visible = true
  X = 0
  Y = 0
  centerLine_color = rgb(0,0,255)
  centerLine_len_dash = 6
  centerLine_len_dot = 3
  centerLine_len_gap = 2
  centerLine_width = 0.32
  click1_x = 257.657
  click1_y = 151.634
  click2_x = 241.727
  click2_y = 149.981
FEATURE [Drawing::FeatureViewPython] centerLines010  # drawing view (typed FeaturePython)
  Rotation = 0
  ViewResult = <g transform="scale(1.000000,1.000000)" stroke="rgb(0,0,255)"  stroke-width="0.320000" > <path d="M 164.978800,166.623000 L 167.978800,166.623000 M 169.978800,166.623000 L 175.978800,166.623000 M 177.978800,166.623000 L 180.978800,166.623000 M 182.978800,166.623000 L 188.978800,166.623000 M 190.978800,166.623000 L 193.978800,166.623000 M 195.978800,166.623000 L 201.978800,166.623000 M 203.978800,166.623000 L 206.978800,166.623000 M 208.978800,166.623000 L 214.978800,166.623000 M 216.978800,166.623000 L 219.978800,166.623000 M 221.978800,166.623000 L 227.978800,166.623000 M 229.978800,166.623000 L 232.978800,166.623000 M 234.978800,166.623000 L 240.978800,166.623000 M 242.978800,166.623000 L 245.978800,166.623000 M 247.978800,166.623000 L 253.978800,166.623000 M 255.978800,166.623000 L 257.644288,166.623000 "/>\n<path d="M 164.978800,166.623000 L 167.978800,166.623000 M 169.978800,166.623000 L 175.978800,166.623000 M 177.978800,166.623000 L 180.978800,166.623000 M 182.978800,166.623000 L 188.978800,166.623000 M 190.978800,166.623000 L 193.978800,166.623000 M 195.978800,166.623000 L 201.978800,166.623000 M 203.978800,166.623000 L 206.978800,166.623000 M 208.978800,166.623000 L 214.978800,166.623000 M 216.978800,166.623000 L 219.978800,166.623000 M 221.978800,166.623000 L 227.978800,166.623000 M 229.978800,166.623000 L 232.978800,166.623000 M 234.978800,166.623000 L 240.978800,166.623000 M 242.978800,166.623000 L 243.296994,166.623000 "/> </g> 
  Visible = true
  X = 0
  Y = 0
  centerLine_color = rgb(0,0,255)
  centerLine_len_dash = 6
  centerLine_len_dot = 3
  centerLine_len_gap = 2
  centerLine_width = 0.32
  click1_x = 257.644
  click1_y = 167.146
  click2_x = 243.297
  click2_y = 168.47
FEATURE [Drawing::FeatureViewPython] centerLines011  # drawing view (typed FeaturePython)
  Rotation = 0
  ViewResult = <g transform="scale(1.000000,1.000000)" stroke="rgb(0,0,255)"  stroke-width="0.320000" > <path d="M 164.981900,205.919900 L 167.981900,205.919900 M 169.981900,205.919900 L 175.981900,205.919900 M 177.981900,205.919900 L 180.981900,205.919900 M 182.981900,205.919900 L 188.981900,205.919900 M 190.981900,205.919900 L 193.981900,205.919900 M 195.981900,205.919900 L 201.981900,205.919900 M 203.981900,205.919900 L 206.981900,205.919900 M 208.981900,205.919900 L 214.981900,205.919900 M 216.981900,205.919900 L 219.981900,205.919900 M 221.981900,205.919900 L 227.981900,205.919900 M 229.981900,205.919900 L 232.981900,205.919900 M 234.981900,205.919900 L 240.981900,205.919900 M 242.981900,205.919900 L 245.981900,205.919900 M 247.981900,205.919900 L 253.981900,205.919900 M 255.981900,205.919900 L 257.511641,205.919900 "/>\n<path d="M 164.981900,205.919900 L 167.981900,205.919900 M 169.981900,205.919900 L 175.981900,205.919900 M 177.981900,205.919900 L 180.981900,205.919900 M 182.981900,205.919900 L 188.981900,205.919900 M 190.981900,205.919900 L 193.981900,205.919900 M 195.981900,205.919900 L 201.981900,205.919900 M 203.981900,205.919900 L 206.981900,205.919900 M 208.981900,205.919900 L 214.981900,205.919900 M 216.981900,205.919900 L 219.981900,205.919900 M 221.981900,205.919900 L 227.981900,205.919900 M 229.981900,205.919900 L 232.981900,205.919900 M 234.981900,205.919900 L 235.870991,205.919900 "/> </g> 
  Visible = true
  X = 0
  Y = 0
  centerLine_color = rgb(0,0,255)
  centerLine_len_dash = 6
  centerLine_len_dot = 3
  centerLine_len_gap = 2
  centerLine_width = 0.32
  click1_x = 257.512
  click1_y = 211.389
  click2_x = 235.871
  click2_y = 210.543
FEATURE [Drawing::FeatureViewPython] centerLines012  # drawing view (typed FeaturePython)
  Rotation = 0
  ViewResult = <g transform="scale(1.000000,1.000000)" stroke="rgb(0,0,255)"  stroke-width="0.320000" > <path d="M 164.959100,242.650500 L 167.959100,242.650500 M 169.959100,242.650500 L 175.959100,242.650500 M 177.959100,242.650500 L 180.959100,242.650500 M 182.959100,242.650500 L 188.959100,242.650500 M 190.959100,242.650500 L 193.959100,242.650500 M 195.959100,242.650500 L 201.959100,242.650500 M 203.959100,242.650500 L 206.959100,242.650500 M 208.959100,242.650500 L 214.959100,242.650500 M 216.959100,242.650500 L 219.959100,242.650500 M 221.959100,242.650500 L 227.959100,242.650500 M 229.959100,242.650500 L 232.959100,242.650500 M 234.959100,242.650500 L 240.959100,242.650500 M 242.959100,242.650500 L 245.959100,242.650500 M 247.959100,242.650500 L 253.959100,242.650500 M 255.959100,242.650500 L 257.656718,242.650500 "/>\n<path d="M 164.959100,242.650500 L 167.959100,242.650500 M 169.959100,242.650500 L 175.959100,242.650500 M 177.959100,242.650500 L 180.959100,242.650500 M 182.959100,242.650500 L 188.959100,242.650500 M 190.959100,242.650500 L 193.959100,242.650500 M 195.959100,242.650500 L 201.959100,242.650500 M 203.959100,242.650500 L 206.959100,242.650500 M 208.959100,242.650500 L 214.959100,242.650500 M 216.959100,242.650500 L 219.959100,242.650500 M 221.959100,242.650500 L 227.959100,242.650500 M 229.959100,242.650500 L 232.959100,242.650500 M 234.959100,242.650500 L 238.767695,242.650500 "/> </g> 
  Visible = true
  X = 0
  Y = 0
  centerLine_color = rgb(0,0,255)
  centerLine_len_dash = 6
  centerLine_len_dot = 3
  centerLine_len_gap = 2
  centerLine_width = 0.32
  click1_x = 257.657
  click1_y = 244.6
  click2_x = 238.768
  click2_y = 244.687
FEATURE [Drawing::FeatureViewPython] centerLines013  # drawing view (typed FeaturePython)
  Rotation = 0
  ViewResult = <g transform="scale(1.000000,1.000000)" stroke="rgb(0,0,255)"  stroke-width="0.320000" > <path d="M 349.972000,136.262000 L 352.972000,136.262000 M 354.972000,136.262000 L 360.972000,136.262000 M 362.972000,136.262000 L 363.750305,136.262000 "/>\n<path d="M 349.972000,136.262000 L 352.972000,136.262000 "/> </g> 
  Visible = true
  X = 0
  Y = 0
  centerLine_color = rgb(0,0,255)
  centerLine_len_dash = 6
  centerLine_len_dot = 3
  centerLine_len_gap = 2
  centerLine_width = 0.32
  click1_x = 363.75
  click1_y = 136.312
  click2_x = 353.222
  click2_y = 136.715
FEATURE [Drawing::FeatureViewPython] centerLines014  # drawing view (typed FeaturePython)
  Rotation = 0
  ViewResult = <g transform="scale(1.000000,1.000000)" stroke="rgb(0,0,255)"  stroke-width="0.320000" > <path d="M 349.973000,264.243900 L 352.973000,264.243900 M 354.973000,264.243900 L 360.973000,264.243900 M 362.973000,264.243900 L 364.796500,264.243900 "/>\n<path d="M 349.973000,264.243900 L 352.973000,264.243900 "/> </g> 
  Visible = true
  X = 0
  Y = 0
  centerLine_color = rgb(0,0,255)
  centerLine_len_dash = 6
  centerLine_len_dot = 3
  centerLine_len_gap = 2
  centerLine_width = 0.32
  click1_x = 364.796
  click1_y = 264.41
  click2_x = 354.334
  click2_y = 264.41
FEATURE [Drawing::FeatureViewPython] dim016  label="dimLength"  # drawing view (typed FeaturePython)
  Rotation = 0
  ViewResult = <g> \n  <line x1="120.000000" y1="297.670000" x2="120.000000" y2="319.660113" style="stroke:rgb(0,0,255);stroke-width:0.50" />\n<line x1="390.000000" y1="297.670000" x2="390.000000" y2="319.660113" style="stroke:rgb(0,0,255);stroke-width:0.50" />\n<line x1="120.000000" y1="318.660113" x2="390.000000" y2="318.660113" style="stroke:rgb(0,0,255);stroke-width:0.50" /> \n  <polygon points="390.000000,318.660113 387.000000,317.660113 386.000000,318.660113 387.000000,319.660113" style="fill:rgb(0,0,255);stroke:rgb(0,0,255);stroke-width:0" /><polygon points="120.000000,318.660113 123.000000,319.660113 124.000000,318.660113 123.000000,317.660113" style="fill:rgb(0,0,255);stroke:rgb(0,0,255);stroke-width:0" /> \n  <text x="247.182518" y="316.580765" font-family="inherit" font-size="6" fill="rgb(0,0,255)" text-anchor="inherit" transform="rotate(0.000000 247.182518,316.580765)" >270mm</text> </g>
  Visible = true
  X = 0
  Y = 0
  arrowL1 = 3
  arrowL2 = 1
  arrowW = 2
  arrow_scheme = 0
  autoPlaceOffset = 2
  autoPlaceText = false
  click1_x = 262.778
  click1_y = 318.66
  click2_x = 247.183
  click2_y = 316.581
  comma_decimal_place = false
  dimension_line_overshoot = 1
  gap_datum_points = 0
  halfDimension_linear = false
  lineColor = rgb(0,0,255)
  strokeWidth = 0.5
  textFormat_linear = %(value)3.0fmm
  textRenderer_color = rgb(0,0,255)
  textRenderer_family = inherit
  textRenderer_size = 6
  unit_custom_scale = 1
  unit_scheme = 0
FEATURE [Drawing::FeatureViewPython] dim017  label="dimHeight"  # drawing view (typed FeaturePython)
  Rotation = 0
  ViewResult = <g> \n  <line x1="120.000000" y1="348.330000" x2="110.161955" y2="348.330000" style="stroke:rgb(0,0,255);stroke-width:0.50" />\n<line x1="120.000000" y1="353.330000" x2="110.161955" y2="353.330000" style="stroke:rgb(0,0,255);stroke-width:0.50" />\n<line x1="111.161955" y1="348.330000" x2="111.161955" y2="353.330000" style="stroke:rgb(0,0,255);stroke-width:0.50" /> \n  <polygon points="111.161955,353.330000 110.161955,356.330000 111.161955,357.330000 112.161955,356.330000" style="fill:rgb(0,0,255);stroke:rgb(0,0,255);stroke-width:0" /><polygon points="111.161955,348.330000 112.161955,345.330000 111.161955,344.330000 110.161955,345.330000" style="fill:rgb(0,0,255);stroke:rgb(0,0,255);stroke-width:0" /> \n  <text x="108.167694" y="358.950000" font-family="inherit" font-size="6" fill="rgb(0,0,255)" text-anchor="inherit" transform="rotate(-90.000000 108.167694,358.950000)" >6mm</text> </g>
  Visible = true
  X = 0
  Y = 0
  arrowL1 = 3
  arrowL2 = 1
  arrowW = 2
  arrow_scheme = 0
  autoPlaceOffset = 2
  autoPlaceText = false
  click1_x = 111.162
  click1_y = 355.194
  click2_x = 108.168
  click2_y = 358.95
  comma_decimal_place = false
  dimension_line_overshoot = 1
  gap_datum_points = 0
  halfDimension_linear = false
  lineColor = rgb(0,0,255)
  strokeWidth = 0.5
  textFormat_linear = 6mm
  textRenderer_color = rgb(0,0,255)
  textRenderer_family = inherit
  textRenderer_size = 6
  unit_custom_scale = 1
  unit_scheme = 0
FEATURE [Drawing::FeatureViewPython] text001  label="title"  # drawing view (typed FeaturePython)
  Rotation = 0
  ViewResult = <g> <text x="288.590000" y="34.550000" font-family="inherit" font-size="30" fill="rgb(0,0,0)" text-anchor="inherit" transform="rotate(0.000000 288.590000,34.550000)" >1/4U TestBed Specs</text> </g>
  Visible = true
  X = 0
  Y = 0
  click1_x = 288.59
  click1_y = 34.55
  rotation = 0
  text = 1/4U TestBed Specs
  textRenderer_addText_color = rgb(0,0,0)
  textRenderer_addText_family = inherit
  textRenderer_addText_size = 30
FEATURE [Drawing::FeatureViewPython] text002  label="caption"  # drawing view (typed FeaturePython)
  Rotation = 0
  ViewResult = <g> <text x="116.610000" y="385.730000" font-family="inherit" font-size="15" fill="rgb(0,0,0)" text-anchor="inherit" transform="rotate(0.000000 116.610000,385.730000)" >*Diameter of the holes are all 3.2mm</text> </g>
  Visible = true
  X = 0
  Y = 0
  click1_x = 116.61
  click1_y = 385.73
  rotation = 0
  text = *Diameter of the holes are all 3.2mm
  textRenderer_addText_color = rgb(0,0,0)
  textRenderer_addText_family = inherit
  textRenderer_addText_size = 15
FEATURE [Drawing::FeatureViewPython] dia001  # drawing view (typed FeaturePython)
  Rotation = 0
  ViewResult = <g>  <circle cx ="257.500000" cy ="242.699000" r="0.250000" stroke="none" fill="rgb(0,0,255)" /> \n<line x1="275.260939" y1="225.443222" x2="256.379610" y2="243.787523" style="stroke:rgb(0,0,255);stroke-width:0.50" />\n<polygon points="258.620390,241.610477 261.468922,240.237210 261.489322,238.823143 260.075256,238.802743" style="fill:rgb(0,0,255);stroke:rgb(0,0,255);stroke-width:0" />\n<polygon points="256.379610,243.787523 253.531078,245.160790 253.510678,246.574857 254.924744,246.595257" style="fill:rgb(0,0,255);stroke:rgb(0,0,255);stroke-width:0" />\n<line x1="275.260939" y1="225.443222" x2="322.732170" y2="225.443222" style="stroke:rgb(0,0,255);stroke-width:0.50" />\n<text x="288.770000" y="223.560000" font-family="inherit" font-size="6" fill="rgb(0,0,255)" text-anchor="inherit" transform="rotate(0.000000 288.770000,223.560000)" >Ø3.2mm</text> </g>
  Visible = true
  X = 0
  Y = 0
  arrowL1 = 3
  arrowL2 = 1
  arrowW = 2
  arrow_scheme = 0
  autoPlaceOffset = 2
  autoPlaceText = false
  centerPointDia = 0.5
  click1_x = 275.261
  click1_y = 225.443
  click2_x = 322.732
  click2_y = 225.624
  click3_x = 288.77
  click3_y = 223.56
  comma_decimal_place = false
  lineColor = rgb(0,0,255)
  strokeWidth = 0.5
  textFormat_circular = Ø3.2mm
  textRenderer_color = rgb(0,0,255)
  textRenderer_family = inherit
  textRenderer_size = 6
  unit_custom_scale = 1
  unit_scheme = 0
FEATURE [Drawing::FeatureViewPython] dim009  # drawing view (typed FeaturePython)
  Rotation = 0
  ViewResult = <g> \n  <line x1="120.000000" y1="102.670000" x2="94.000000" y2="102.670000" style="stroke:rgb(0,0,255);stroke-width:0.50" />\n<line x1="222.965000" y1="161.647000" x2="94.000000" y2="161.647000" style="stroke:rgb(0,0,255);stroke-width:0.50" />\n<line x1="95.000000" y1="102.670000" x2="95.000000" y2="161.647000" style="stroke:rgb(0,0,255);stroke-width:0.50" /> \n  <polygon points="95.000000,161.647000 96.000000,158.647000 95.000000,157.647000 94.000000,158.647000" style="fill:rgb(0,0,255);stroke:rgb(0,0,255);stroke-width:0" /><polygon points="95.000000,102.670000 94.000000,105.670000 95.000000,106.670000 96.000000,105.670000" style="fill:rgb(0,0,255);stroke:rgb(0,0,255);stroke-width:0" /> \n  <text x="93.000000" y="139.354446" font-family="inherit" font-size="6" fill="rgb(0,0,255)" text-anchor="inherit" transform="rotate(-90.000000 93.000000,139.354446)" >59mm</text> </g>
  Visible = true
  X = 0
  Y = 0
  arrowL1 = 3
  arrowL2 = 1
  arrowW = 2
  arrow_scheme = 0
  autoPlaceOffset = 2
  autoPlaceText = false
  click1_x = 95
  click1_y = 142.733
  click2_x = 93
  click2_y = 139.354
  comma_decimal_place = false
  dimension_line_overshoot = 1
  gap_datum_points = 0
  halfDimension_linear = false
  lineColor = rgb(0,0,255)
  strokeWidth = 0.5
  textFormat_linear = 59mm
  textRenderer_color = rgb(0,0,255)
  textRenderer_family = inherit
  textRenderer_size = 6
  unit_custom_scale = 1
  unit_scheme = 0
FEATURE [App::DocumentObjectGroup] Group002  label="LeftDim"
  Group = -> [dim007,dim008,dim010,dim011,dim012,dim009]
FEATURE [Drawing::FeatureViewPython] centerLines009  # drawing view (typed FeaturePython)
  Rotation = 0
  ViewResult = <g transform="scale(1.000000,1.000000)" stroke="rgb(0,0,255)"  stroke-width="0.320000" > <path d="M 222.965000,161.647000 L 225.965000,161.647000 M 227.965000,161.647000 L 233.965000,161.647000 M 235.965000,161.647000 L 238.965000,161.647000 M 240.965000,161.647000 L 246.965000,161.647000 M 248.965000,161.647000 L 251.965000,161.647000 M 253.965000,161.647000 L 259.965000,161.647000 M 261.965000,161.647000 L 264.965000,161.647000 M 266.965000,161.647000 L 272.965000,161.647000 M 274.965000,161.647000 L 277.965000,161.647000 M 279.965000,161.647000 L 285.965000,161.647000 M 287.965000,161.647000 L 290.965000,161.647000 M 292.965000,161.647000 L 298.965000,161.647000 M 300.965000,161.647000 L 303.965000,161.647000 M 305.965000,161.647000 L 311.965000,161.647000 M 313.965000,161.647000 L 315.410539,161.647000 "/>\n<path d="M 222.965000,161.647000 L 225.965000,161.647000 M 227.965000,161.647000 L 233.965000,161.647000 M 235.965000,161.647000 L 238.965000,161.647000 M 240.965000,161.647000 L 246.965000,161.647000 M 248.965000,161.647000 L 251.965000,161.647000 M 253.965000,161.647000 L 259.965000,161.647000 M 261.965000,161.647000 L 264.965000,161.647000 M 266.965000,161.647000 L 272.965000,161.647000 M 274.965000,161.647000 L 277.965000,161.647000 M 279.965000,161.647000 L 285.965000,161.647000 M 287.965000,161.647000 L 290.965000,161.647000 M 292.965000,161.647000 L 298.965000,161.647000 M 300.965000,161.647000 L 303.546431,161.647000 "/> </g> 
  Visible = true
  X = 0
  Y = 0
  centerLine_color = rgb(0,0,255)
  centerLine_len_dash = 6
  centerLine_len_dot = 3
  centerLine_len_gap = 2
  centerLine_width = 0.32
  click1_x = 315.411
  click1_y = 161.913
  click2_x = 303.546
  click2_y = 161.821
FEATURE [App::DocumentObjectGroup] Group004  label="centerLines"
  Group = -> [centerLines001,centerLines002,centerLines003,centerLines004,centerLines005,centerLines006,centerLines007,centerLines008,centerLines010,centerLines011,centerLines012,centerLines013,centerLines014,centerLines009]
FEATURE [Drawing::FeaturePage] Page  label="1/4Upage"
  EditableTexts = Jimmy Huang | 1/4U TestBed | FreeCAD DRAWING | A2 | X / Y | 1:1 | N/A | N/A | 13/07/2017 | VER 1
  Group = -> [Ortho,Ortho001,Group001,Group002,Group003,Group004,dim016,dim017,text001,text002,dia001]
